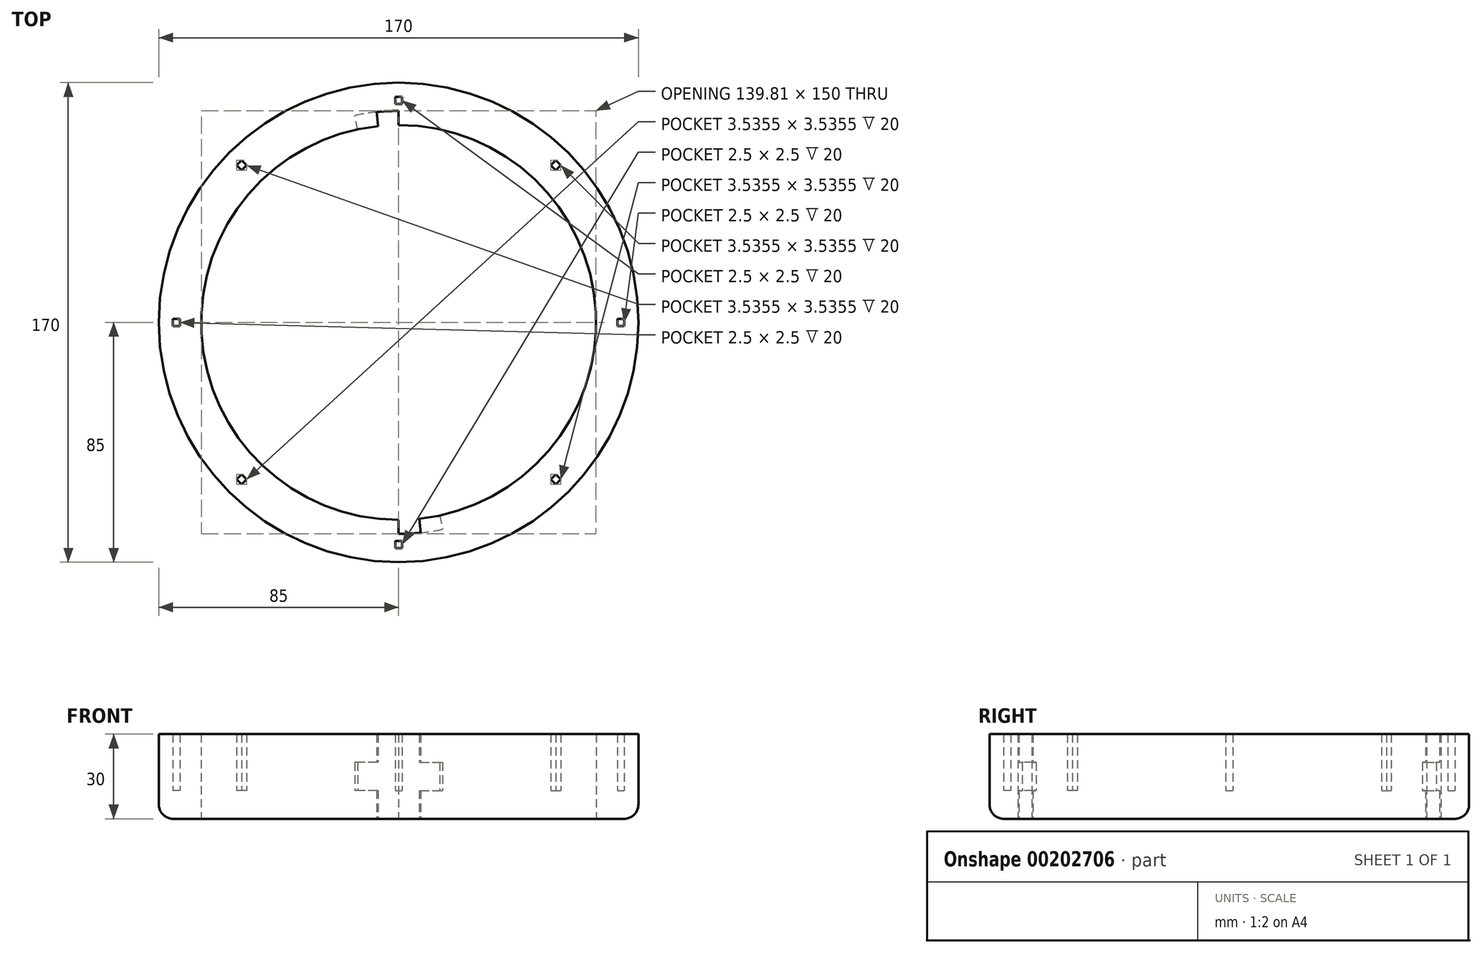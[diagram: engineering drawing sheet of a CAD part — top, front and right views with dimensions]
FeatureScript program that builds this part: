
annotation { "Feature Type Name" : "Feature", "Feature Type Description" : "" }
export const myFeature = defineFeature(function(context is Context, id is Id, definition is map)
    precondition{}
    {
        {
            var Q0;
            Q0=qCreatedBy(makeId("Top.planeOp"),FACE);
            var sketch = newSketch(context, id + "F0", { "sketchPlane" : qUnion([Q0])});
            skCircle(sketch, "E0", {"center": v(0, 0) * mm, "radius": 70 * mm});
            skCircle(sketch, "E1", {"center": v(0, 0) * mm, "radius": 75 * mm});
            skCircle(sketch, "E2", {"center": v(0, 0) * mm, "radius": 85 * mm});
            skLineSegment(sketch, "E3", {"start": v(0, 0) * mm, "end": v(0, 75) * mm});
            skLineSegment(sketch, "E4", {"start": v(0, 0) * mm, "end": v(-7.84, 74.59) * mm});
            skLineSegment(sketch, "E5", {"start": v(0, 0) * mm, "end": v(-15.6, 73.36) * mm});
            skLineSegment(sketch, "E6", {"start": v(0, 0) * mm, "end": v(0, -75) * mm});
            skLineSegment(sketch, "E7", {"start": v(0, 0) * mm, "end": v(7.84, -74.59) * mm});
            skLineSegment(sketch, "E8", {"start": v(0, 0) * mm, "end": v(15.6, -73.36) * mm});
            skSolve(sketch);
        }
        {
            var Q0;
            {var subQ0=sQuery(id+"F0.wireOp",EDGE,"E5");var subQ1=sQuery(id+"F0.wireOp",EDGE,"E0");var subQ2=makeQuery(id+"F0.imprint","INTERSECT",VERTEX,{"derivedFrom":[subQ1,subQ0]});Q0=makeQuery(id+"F0.imprint","IMPRINT",FACE,{"disambiguationData":[TD([[makeQuery(id+"F0.imprint","IMPRINT",EDGE,{"disambiguationData":[TD([[subQ2,-1.0]])],"derivedFrom":subQ1}),-1.0]])]});}
            var Q1;
            {var subQ0=sQuery(id+"F0.wireOp",EDGE,"E3");var subQ1=sQuery(id+"F0.wireOp",EDGE,"E0");var subQ2=makeQuery(id+"F0.imprint","INTERSECT",VERTEX,{"derivedFrom":[subQ1,subQ0]});Q1=makeQuery(id+"F0.imprint","IMPRINT",FACE,{"disambiguationData":[TD([[makeQuery(id+"F0.imprint","IMPRINT",EDGE,{"disambiguationData":[TD([[subQ2,1.0]])],"derivedFrom":subQ1}),-1.0]])]});}
            var Q2;
            Q2=makeQuery(id+"F0.imprint","IMPRINT",FACE,{"disambiguationData":[TD([[makeQuery(id+"F0.imprint","IMPRINT",EDGE,{"derivedFrom":sQuery(id+"F0.wireOp",EDGE,"E2")}),1.0]])]});
            extrude(context, id + "F1", {"entities" : qUnion([Q0, Q1, Q2]), "depth" : 30 * mm});
        }
        {
            var Q0;
            {var subQ0=sQuery(id+"F0.wireOp",EDGE,"E4");var subQ1=sQuery(id+"F0.wireOp",EDGE,"E0");var subQ2=makeQuery(id+"F0.imprint","INTERSECT",VERTEX,{"derivedFrom":[subQ1,subQ0]});Q0=makeQuery(id+"F0.imprint","IMPRINT",FACE,{"disambiguationData":[TD([[makeQuery(id+"F0.imprint","IMPRINT",EDGE,{"disambiguationData":[TD([[subQ2,-1.0]])],"derivedFrom":subQ1}),-1.0]])]});}
            var Q1;
            {var subQ0=sQuery(id+"F0.wireOp",EDGE,"E7");var subQ1=sQuery(id+"F0.wireOp",EDGE,"E0");var subQ2=makeQuery(id+"F0.imprint","INTERSECT",VERTEX,{"derivedFrom":[subQ1,subQ0]});Q1=makeQuery(id+"F0.imprint","IMPRINT",FACE,{"disambiguationData":[TD([[makeQuery(id+"F0.imprint","IMPRINT",EDGE,{"disambiguationData":[TD([[subQ2,-1.0]])],"derivedFrom":subQ1}),-1.0]])]});}
            extrude(context, id + "F2", {"entities" : qUnion([Q0, Q1]), "operationType" : NewBodyOperationType.ADD, "depth" : 10 * mm});
        }
        {
            var Q0;
            {var subQ0=sQuery(id+"F0.wireOp",EDGE,"E5");var subQ1=sQuery(id+"F0.wireOp",EDGE,"E0");var subQ2=makeQuery(id+"F0.imprint","INTERSECT",VERTEX,{"derivedFrom":[subQ1,subQ0]});Q0=makeQuery(id+"F0.imprint","IMPRINT",FACE,{"disambiguationData":[TD([[makeQuery(id+"F0.imprint","IMPRINT",EDGE,{"disambiguationData":[TD([[subQ2,-1.0]])],"derivedFrom":subQ1}),1.0]])]});}
            cPlane(context, id + "F3", {"entities" : qUnion([Q0]), "cplaneType" : CPlaneType.OFFSET, "offset" : 20 * mm, "width" : 150 * mm, "height" : 150 * mm});
        }
        {
            var Q0;
            Q0=qCreatedBy(id+"F3.planeOp",FACE);
            var sketch = newSketch(context, id + "F4", { "sketchPlane" : qUnion([Q0])});
            skCircle(sketch, "E9", {"center": v(0, 0) * mm, "radius": 75 * mm});
            skLineSegment(sketch, "E10", {"start": v(0, 0) * mm, "end": v(-7.84, 74.59) * mm});
            skLineSegment(sketch, "E11", {"start": v(0, 0) * mm, "end": v(-15.6, 73.36) * mm});
            skLineSegment(sketch, "E12", {"start": v(0, 0) * mm, "end": v(7.84, -74.59) * mm});
            skLineSegment(sketch, "E13", {"start": v(0, 0) * mm, "end": v(15.6, -73.36) * mm});
            skCircle(sketch, "E14", {"center": v(0, 0) * mm, "radius": 70 * mm});
            skSolve(sketch);
        }
        {
            var Q0;
            {var subQ0=sQuery(id+"F4.wireOp",EDGE,"E10");var subQ1=sQuery(id+"F4.wireOp",EDGE,"E9");var subQ2=makeQuery(id+"F4.imprint","INTERSECT",VERTEX,{"derivedFrom":[subQ1,subQ0]});Q0=makeQuery(id+"F4.imprint","IMPRINT",FACE,{"disambiguationData":[TD([[makeQuery(id+"F4.imprint","IMPRINT",EDGE,{"disambiguationData":[TD([[subQ2,-1.0]])],"derivedFrom":subQ1}),1.0]])]});}
            var Q1;
            {var subQ0=sQuery(id+"F4.wireOp",EDGE,"E12");var subQ1=sQuery(id+"F4.wireOp",EDGE,"E9");var subQ2=makeQuery(id+"F4.imprint","INTERSECT",VERTEX,{"derivedFrom":[subQ1,subQ0]});Q1=makeQuery(id+"F4.imprint","IMPRINT",FACE,{"disambiguationData":[TD([[makeQuery(id+"F4.imprint","IMPRINT",EDGE,{"disambiguationData":[TD([[subQ2,-1.0]])],"derivedFrom":subQ1}),1.0]])]});}
            extrude(context, id + "F5", {"entities" : qUnion([Q0, Q1]), "operationType" : NewBodyOperationType.ADD, "depth" : 10 * mm});
        }
        {
            var Q0;
            {var subQ0=sQuery(id+"F4.wireOp",EDGE,"E14");var subQ1=sQuery(id+"F4.wireOp",EDGE,"E9");Q0=makeQuery(id+"F5.boolean.opBoolean","MERGE",FACE,{"derivedFrom":[makeQuery(id+"F1.opExtrude","CAP_FACE",FACE,{"disambiguationData":[OSD([sQuery(id+"F0.wireOp",EDGE,"E0"),sQuery(id+"F0.wireOp",EDGE,"E1"),sQuery(id+"F0.wireOp",EDGE,"E2"),sQuery(id+"F0.wireOp",EDGE,"E3"),sQuery(id+"F0.wireOp",EDGE,"E5"),sQuery(id+"F0.wireOp",EDGE,"E6"),sQuery(id+"F0.wireOp",EDGE,"E8")])],"isStart":false}),makeQuery(id+"F5.opExtrude","CAP_FACE",FACE,{"disambiguationData":[OSD([subQ1,sQuery(id+"F4.wireOp",EDGE,"E10"),sQuery(id+"F4.wireOp",EDGE,"E11"),subQ0])],"isStart":false}),makeQuery(id+"F5.opExtrude","CAP_FACE",FACE,{"disambiguationData":[OSD([subQ1,sQuery(id+"F4.wireOp",EDGE,"E12"),sQuery(id+"F4.wireOp",EDGE,"E13"),subQ0])],"isStart":false})]});}
            var sketch = newSketch(context, id + "F6", { "sketchPlane" : qUnion([Q0])});
            skLineSegment(sketch, "E15.bottom", {"start": v(1.25, 77.5) * mm, "end": v(-1.25, 77.5) * mm});
            skPoint(sketch, "E15.middle", {"position": v(0, 0) * mm});
            skLineSegment(sketch, "E16.top", {"start": v(-1.25, 80) * mm, "end": v(1.25, 80) * mm});
            skLineSegment(sketch, "E16.left", {"start": v(-1.25, 77.5) * mm, "end": v(-1.25, 80) * mm});
            skLineSegment(sketch, "E16.right", {"start": v(1.25, 77.5) * mm, "end": v(1.25, 80) * mm});
            skSolve(sketch);
        }
        {
            var Q0;
            Q0=makeQuery(id+"F6.imprint","IMPRINT",FACE,{"disambiguationData":[TD([[makeQuery(id+"F6.imprint","IMPRINT",EDGE,{"derivedFrom":sQuery(id+"F6.wireOp",EDGE,"E15.bottom")}),-1.0]])]});
            extrude(context, id + "F7", {"entities" : qUnion([Q0]), "endBound" : BoundingType.SYMMETRIC, "depth" : 40 * mm});
        }
        {
            var Q0;
            Q0=qCreatedBy(makeId("Right.planeOp"),FACE);
            var sketch = newSketch(context, id + "F8", { "sketchPlane" : qUnion([Q0])});
            skLineSegment(sketch, "E17", {"start": v(0, 0) * mm, "end": v(0, 22.53) * mm});
            skSolve(sketch);
        }
        {
            var Q0;
            Q0=makeQuery(id+"F7.opExtrude","SWEPT_BODY",BODY,{"disambiguationData":[OSD([sQuery(id+"F6.wireOp",EDGE,"E15.bottom"),sQuery(id+"F6.wireOp",EDGE,"E16.top"),sQuery(id+"F6.wireOp",EDGE,"E16.left"),sQuery(id+"F6.wireOp",EDGE,"E16.right")])]});
            var Q1;
            Q1=sQuery(id+"F8.wireOp",EDGE,"E17");
            circularPattern(context, id + "F9", {"entities" : qUnion([Q0]), "axis" : qUnion([Q1]), "angle" : 360 * degree, "instanceCount" : 8, "equalSpace" : true});
        }
        {
            var Q0;
            Q0=makeQuery(id+"F9.opPattern","COPY",BODY,{"derivedFrom":makeQuery(id+"F7.opExtrude","SWEPT_BODY",BODY,{"disambiguationData":[OSD([sQuery(id+"F6.wireOp",EDGE,"E15.bottom"),sQuery(id+"F6.wireOp",EDGE,"E16.top"),sQuery(id+"F6.wireOp",EDGE,"E16.left"),sQuery(id+"F6.wireOp",EDGE,"E16.right")])]}),"instanceName":"2"});
            var Q1;
            Q1=makeQuery(id+"F9.opPattern","COPY",BODY,{"derivedFrom":makeQuery(id+"F7.opExtrude","SWEPT_BODY",BODY,{"disambiguationData":[OSD([sQuery(id+"F6.wireOp",EDGE,"E15.bottom"),sQuery(id+"F6.wireOp",EDGE,"E16.top"),sQuery(id+"F6.wireOp",EDGE,"E16.left"),sQuery(id+"F6.wireOp",EDGE,"E16.right")])]}),"instanceName":"1"});
            var Q2;
            Q2=makeQuery(id+"F7.opExtrude","SWEPT_BODY",BODY,{"disambiguationData":[OSD([sQuery(id+"F6.wireOp",EDGE,"E15.bottom"),sQuery(id+"F6.wireOp",EDGE,"E16.top"),sQuery(id+"F6.wireOp",EDGE,"E16.left"),sQuery(id+"F6.wireOp",EDGE,"E16.right")])]});
            var Q3;
            Q3=makeQuery(id+"F9.opPattern","COPY",BODY,{"derivedFrom":makeQuery(id+"F7.opExtrude","SWEPT_BODY",BODY,{"disambiguationData":[OSD([sQuery(id+"F6.wireOp",EDGE,"E15.bottom"),sQuery(id+"F6.wireOp",EDGE,"E16.top"),sQuery(id+"F6.wireOp",EDGE,"E16.left"),sQuery(id+"F6.wireOp",EDGE,"E16.right")])]}),"instanceName":"7"});
            var Q4;
            Q4=makeQuery(id+"F9.opPattern","COPY",BODY,{"derivedFrom":makeQuery(id+"F7.opExtrude","SWEPT_BODY",BODY,{"disambiguationData":[OSD([sQuery(id+"F6.wireOp",EDGE,"E15.bottom"),sQuery(id+"F6.wireOp",EDGE,"E16.top"),sQuery(id+"F6.wireOp",EDGE,"E16.left"),sQuery(id+"F6.wireOp",EDGE,"E16.right")])]}),"instanceName":"6"});
            var Q5;
            Q5=makeQuery(id+"F9.opPattern","COPY",BODY,{"derivedFrom":makeQuery(id+"F7.opExtrude","SWEPT_BODY",BODY,{"disambiguationData":[OSD([sQuery(id+"F6.wireOp",EDGE,"E15.bottom"),sQuery(id+"F6.wireOp",EDGE,"E16.top"),sQuery(id+"F6.wireOp",EDGE,"E16.left"),sQuery(id+"F6.wireOp",EDGE,"E16.right")])]}),"instanceName":"5"});
            var Q6;
            Q6=makeQuery(id+"F9.opPattern","COPY",BODY,{"derivedFrom":makeQuery(id+"F7.opExtrude","SWEPT_BODY",BODY,{"disambiguationData":[OSD([sQuery(id+"F6.wireOp",EDGE,"E15.bottom"),sQuery(id+"F6.wireOp",EDGE,"E16.top"),sQuery(id+"F6.wireOp",EDGE,"E16.left"),sQuery(id+"F6.wireOp",EDGE,"E16.right")])]}),"instanceName":"4"});
            var Q7;
            Q7=makeQuery(id+"F9.opPattern","COPY",BODY,{"derivedFrom":makeQuery(id+"F7.opExtrude","SWEPT_BODY",BODY,{"disambiguationData":[OSD([sQuery(id+"F6.wireOp",EDGE,"E15.bottom"),sQuery(id+"F6.wireOp",EDGE,"E16.top"),sQuery(id+"F6.wireOp",EDGE,"E16.left"),sQuery(id+"F6.wireOp",EDGE,"E16.right")])]}),"instanceName":"3"});
            var Q8;
            Q8=makeQuery(id+"F1.opExtrude","SWEPT_BODY",BODY,{"disambiguationData":[OSD([sQuery(id+"F0.wireOp",EDGE,"E0"),sQuery(id+"F0.wireOp",EDGE,"E1"),sQuery(id+"F0.wireOp",EDGE,"E2"),sQuery(id+"F0.wireOp",EDGE,"E3"),sQuery(id+"F0.wireOp",EDGE,"E5"),sQuery(id+"F0.wireOp",EDGE,"E6"),sQuery(id+"F0.wireOp",EDGE,"E8")])]});
            booleanBodies(context, id + "F10", {"operationType" : BooleanOperationType.SUBTRACTION, "tools" : qUnion([Q0, Q1, Q2, Q3, Q4, Q5, Q6, Q7]), "targets" : qUnion([Q8])});
        }
        {
            var Q0;
            Q0=makeQuery(id+"F1.opExtrude","CAP_EDGE",EDGE,{"disambiguationData":[OSD([sQuery(id+"F0.wireOp",EDGE,"E2")])],"isStart":true});
            fillet(context, id + "F11", {"entities" : qUnion([Q0]), "radius" : 5 * mm, "tangentPropagation" : true, "allowEdgeOverflow" : false});
        }
    });
